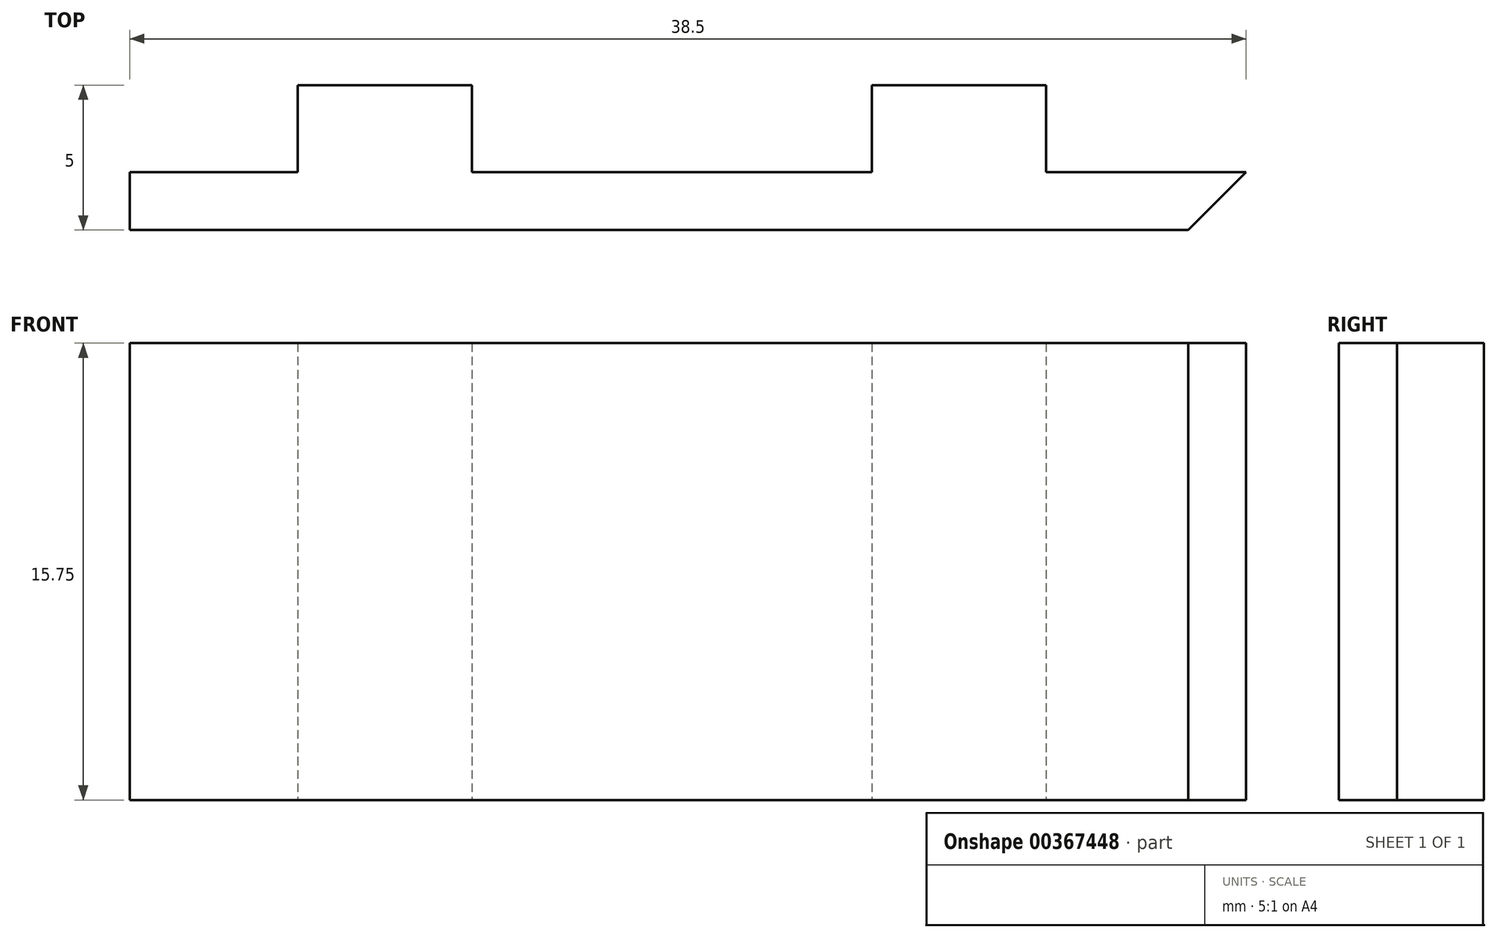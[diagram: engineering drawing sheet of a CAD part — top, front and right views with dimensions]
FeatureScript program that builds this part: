
annotation { "Feature Type Name" : "Feature", "Feature Type Description" : "" }
export const myFeature = defineFeature(function(context is Context, id is Id, definition is map)
    precondition{}
    {
        {
            var Q0;
            Q0=qCreatedBy(makeId("Top.planeOp"),FACE);
            var sketch = newSketch(context, id + "F0", { "sketchPlane" : qUnion([Q0])});
            skLineSegment(sketch, "E0", {"start": v(44.5, 0) * mm, "end": v(44.5, 10) * mm});
            skLineSegment(sketch, "E1", {"start": v(44.5, 10) * mm, "end": v(37.6, 10) * mm});
            skLineSegment(sketch, "E2", {"start": v(37.6, 10) * mm, "end": v(37.6, 16) * mm});
            skLineSegment(sketch, "E3", {"start": v(37.6, 16) * mm, "end": v(31.6, 16) * mm});
            skLineSegment(sketch, "E4", {"start": v(31.6, 16) * mm, "end": v(31.6, 10) * mm});
            skLineSegment(sketch, "E5", {"start": v(31.6, 10) * mm, "end": v(17.8, 10) * mm});
            skLineSegment(sketch, "E6", {"start": v(17.8, 10) * mm, "end": v(17.8, 16) * mm});
            skLineSegment(sketch, "E7", {"start": v(17.8, 16) * mm, "end": v(11.8, 16) * mm});
            skLineSegment(sketch, "E8", {"start": v(11.8, 16) * mm, "end": v(11.8, 10) * mm});
            skLineSegment(sketch, "E9", {"start": v(11.8, 10) * mm, "end": v(0, 10) * mm});
            skLineSegment(sketch, "E10", {"start": v(0, 0) * mm, "end": v(44.5, 0) * mm});
            skLineSegment(sketch, "E11", {"start": v(0, 10) * mm, "end": v(0, 0) * mm});
            skSolve(sketch);
        }
        {
            var Q0;
            Q0=qSketchRegion(id+"F0",true);
            extrude(context, id + "F1", {"entities" : qUnion([Q0]), "depth" : 15.75 * mm});
        }
        {
            var Q0;
            Q0=makeQuery(id+"F1.opExtrude","CAP_FACE",FACE,{"disambiguationData":[OSD([sQuery(id+"F0.wireOp",EDGE,"E0"),sQuery(id+"F0.wireOp",EDGE,"E1"),sQuery(id+"F0.wireOp",EDGE,"E2"),sQuery(id+"F0.wireOp",EDGE,"E3"),sQuery(id+"F0.wireOp",EDGE,"E4"),sQuery(id+"F0.wireOp",EDGE,"E5"),sQuery(id+"F0.wireOp",EDGE,"E6"),sQuery(id+"F0.wireOp",EDGE,"E7"),sQuery(id+"F0.wireOp",EDGE,"E8"),sQuery(id+"F0.wireOp",EDGE,"E9"),sQuery(id+"F0.wireOp",EDGE,"E10"),sQuery(id+"F0.wireOp",EDGE,"E11")])],"isStart":false});
            var sketch = newSketch(context, id + "F2", { "sketchPlane" : qUnion([Q0])});
            skPoint(sketch, "E12", {"position": v(24.7, 5) * mm});
            skPoint(sketch, "E12.positionSnap0", {"position": v(44.5, 5) * mm});
            skPoint(sketch, "E12.positionSnap1", {"position": v(24.7, 10) * mm});
            skSolve(sketch);
        }
        {
            var Q0;
            Q0=sQuery(id+"F2.wireOp",VERTEX,"E12");
            var Q1;
            Q1=makeQuery(id+"F1.opExtrude","SWEPT_BODY",BODY,{"disambiguationData":[OSD([sQuery(id+"F0.wireOp",EDGE,"E0"),sQuery(id+"F0.wireOp",EDGE,"E1"),sQuery(id+"F0.wireOp",EDGE,"E2"),sQuery(id+"F0.wireOp",EDGE,"E3"),sQuery(id+"F0.wireOp",EDGE,"E4"),sQuery(id+"F0.wireOp",EDGE,"E5"),sQuery(id+"F0.wireOp",EDGE,"E6"),sQuery(id+"F0.wireOp",EDGE,"E7"),sQuery(id+"F0.wireOp",EDGE,"E8"),sQuery(id+"F0.wireOp",EDGE,"E9"),sQuery(id+"F0.wireOp",EDGE,"E10"),sQuery(id+"F0.wireOp",EDGE,"E11")])]});
            hole(context, id + "F3", {"style" : HoleStyle.SIMPLE, "endStyle" : HoleEndStyle.THROUGH, "holeDiameter" : 4 * mm, "locations" : qUnion([Q0]), "scope" : qUnion([Q1]), "isTappedThrough" : true});
        }
        {
            var Q0;
            Q0=makeQuery(id+"F1.opExtrude","SWEPT_FACE",FACE,{"disambiguationData":[OSD([sQuery(id+"F0.wireOp",EDGE,"E11")])]});
            extrude(context, id + "F4", {"entities" : qUnion([Q0]), "operationType" : NewBodyOperationType.ADD, "depth" : 3 * mm});
        }
        {
            var Q0;
            {var subQ0=sQuery(id+"F0.wireOp",EDGE,"E9");Q0=makeQuery(id+"F4.boolean.opBoolean","MERGE",FACE,{"derivedFrom":[makeQuery(id+"F1.opExtrude","SWEPT_FACE",FACE,{"disambiguationData":[OSD([subQ0])]}),makeQuery(id+"F4.opExtrude","SWEPT_FACE",FACE,{"disambiguationData":[OSD([subQ0,sQuery(id+"F0.wireOp",EDGE,"E11")])]})]});}
            var sketch = newSketch(context, id + "F5", { "sketchPlane" : qUnion([Q0])});
            skLineSegment(sketch, "E13", {"start": v(0, 0) * mm, "end": v(0, 15.75) * mm});
            skSolve(sketch);
        }
        {
            var Q0;
            {var subQ0=sQuery(id+"F5.wireOp",EDGE,"E13");Q0=makeQuery(id+"F5.imprint","IMPRINT",FACE,{"disambiguationData":[TD([[makeQuery(id+"F5.imprint","IMPRINT",EDGE,{"derivedFrom":subQ0}),-1.0]])]});}
            extrude(context, id + "F6", {"entities" : qUnion([Q0]), "operationType" : NewBodyOperationType.ADD, "depth" : 25 * mm});
        }
        {
            var Q0;
            Q0=makeQuery(id+"F6.opExtrude","SWEPT_FACE",FACE,{"disambiguationData":[OSD([sQuery(id+"F5.wireOp",EDGE,"E13")])]});
            var sketch = newSketch(context, id + "F7", { "sketchPlane" : qUnion([Q0])});
            skPoint(sketch, "E14", {"position": v(27.25, 7.88) * mm});
            skPoint(sketch, "E14.positionSnap0", {"position": v(35, 7.88) * mm});
            skPoint(sketch, "E15", {"position": v(17.75, 7.88) * mm});
            skLineSegment(sketch, "E16", {"start": v(27.25, 7.88) * mm, "end": v(35, 7.88) * mm, "construction": true});
            skLineSegment(sketch, "E17", {"start": v(17.75, 7.88) * mm, "end": v(10, 7.88) * mm, "construction": true});
            skSolve(sketch);
        }
        {
            var Q0;
            Q0=sQuery(id+"F7.wireOp",VERTEX,"E14");
            var Q1;
            Q1=sQuery(id+"F7.wireOp",VERTEX,"E15");
            var Q2;
            Q2=makeQuery(id+"F1.opExtrude","SWEPT_BODY",BODY,{"disambiguationData":[OSD([sQuery(id+"F0.wireOp",EDGE,"E0"),sQuery(id+"F0.wireOp",EDGE,"E1"),sQuery(id+"F0.wireOp",EDGE,"E2"),sQuery(id+"F0.wireOp",EDGE,"E3"),sQuery(id+"F0.wireOp",EDGE,"E4"),sQuery(id+"F0.wireOp",EDGE,"E5"),sQuery(id+"F0.wireOp",EDGE,"E6"),sQuery(id+"F0.wireOp",EDGE,"E7"),sQuery(id+"F0.wireOp",EDGE,"E8"),sQuery(id+"F0.wireOp",EDGE,"E9"),sQuery(id+"F0.wireOp",EDGE,"E10"),sQuery(id+"F0.wireOp",EDGE,"E11")])]});
            hole(context, id + "F8", {"style" : HoleStyle.SIMPLE, "endStyle" : HoleEndStyle.THROUGH, "holeDiameter" : 2 * mm, "startFromSketch" : true, "locations" : qUnion([Q0, Q1]), "scope" : qUnion([Q2]), "isTappedThrough" : true});
        }
        {
            var Q0;
            {var subQ0=sQuery(id+"F0.wireOp",EDGE,"E11");var subQ1=sQuery(id+"F0.wireOp",EDGE,"E9");var subQ2=makeQuery(id+"F4.boolean.opBoolean","MERGE",EDGE,{"derivedFrom":[makeQuery(id+"F1.opExtrude","CAP_EDGE",EDGE,{"disambiguationData":[OSD([subQ1])],"isStart":false}),makeQuery(id+"F4.opExtrude","SWEPT_EDGE",EDGE,{"disambiguationData":[OSD([subQ1,subQ0]),TDD([makeQuery(id+"F1.opExtrude","CAP_VERTEX",VERTEX,{"disambiguationData":[OSD([subQ1,subQ0])],"isStart":false})])]})]});Q0=makeQuery(id+"F6.boolean.opBoolean","MERGE",FACE,{"derivedFrom":[makeQuery(id+"F4.boolean.opBoolean","MERGE",FACE,{"derivedFrom":[makeQuery(id+"F1.opExtrude","CAP_FACE",FACE,{"disambiguationData":[OSD([sQuery(id+"F0.wireOp",EDGE,"E0"),sQuery(id+"F0.wireOp",EDGE,"E1"),sQuery(id+"F0.wireOp",EDGE,"E2"),sQuery(id+"F0.wireOp",EDGE,"E3"),sQuery(id+"F0.wireOp",EDGE,"E4"),sQuery(id+"F0.wireOp",EDGE,"E5"),sQuery(id+"F0.wireOp",EDGE,"E6"),sQuery(id+"F0.wireOp",EDGE,"E7"),sQuery(id+"F0.wireOp",EDGE,"E8"),subQ1,sQuery(id+"F0.wireOp",EDGE,"E10"),subQ0])],"isStart":false}),makeQuery(id+"F4.opExtrude","SWEPT_FACE",FACE,{"disambiguationData":[OSD([subQ0]),TDD([makeQuery(id+"F1.opExtrude","CAP_EDGE",EDGE,{"disambiguationData":[OSD([subQ0])],"isStart":false})])]})]}),makeQuery(id+"F6.opExtrude","SWEPT_FACE",FACE,{"disambiguationData":[OSD([subQ1,subQ0]),TDD([makeQuery(id+"F5.imprint","IMPRINT",EDGE,{"disambiguationData":[TD([[makeQuery(id+"F5.imprint","INTERSECT",VERTEX,{"derivedFrom":[subQ2,sQuery(id+"F5.wireOp",EDGE,"E13")]}),-1.0]])],"derivedFrom":subQ2})])]})]});}
            var sketch = newSketch(context, id + "F9", { "sketchPlane" : qUnion([Q0])});
            skLineSegment(sketch, "E18", {"start": v(0, 10) * mm, "end": v(0, 6) * mm});
            skLineSegment(sketch, "E19", {"start": v(0, 6) * mm, "end": v(6, 6) * mm});
            skLineSegment(sketch, "E20", {"start": v(6, 6) * mm, "end": v(6, 10) * mm});
            skLineSegment(sketch, "E21", {"start": v(6, 10) * mm, "end": v(0, 10) * mm});
            skSolve(sketch);
        }
        {
            var Q0;
            Q0=qSketchRegion(id+"F9",true);
            extrude(context, id + "F10", {"entities" : qUnion([Q0]), "operationType" : NewBodyOperationType.REMOVE, "endBound" : BoundingType.THROUGH_ALL, "oppositeDirection" : true, "depth" : 25 * mm});
        }
        {
            var Q0;
            Q0=makeQuery(id+"F1.opExtrude","SWEPT_EDGE",EDGE,{"disambiguationData":[OSD([sQuery(id+"F0.wireOp",EDGE,"E7"),sQuery(id+"F0.wireOp",EDGE,"E8")])]});
            var Q1;
            Q1=makeQuery(id+"F1.opExtrude","SWEPT_EDGE",EDGE,{"disambiguationData":[OSD([sQuery(id+"F0.wireOp",EDGE,"E6"),sQuery(id+"F0.wireOp",EDGE,"E7")])]});
            var Q2;
            Q2=makeQuery(id+"F1.opExtrude","SWEPT_EDGE",EDGE,{"disambiguationData":[OSD([sQuery(id+"F0.wireOp",EDGE,"E3"),sQuery(id+"F0.wireOp",EDGE,"E4")])]});
            var Q3;
            Q3=makeQuery(id+"F1.opExtrude","SWEPT_EDGE",EDGE,{"disambiguationData":[OSD([sQuery(id+"F0.wireOp",EDGE,"E2"),sQuery(id+"F0.wireOp",EDGE,"E3")])]});
            chamfer(context, id + "F11", {"entities" : qUnion([Q0, Q1, Q2, Q3]), "width" : 1 * mm, "tangentPropagation" : true});
        }
        {
            var Q0;
            Q0=makeQuery(id+"F1.opExtrude","SWEPT_EDGE",EDGE,{"disambiguationData":[OSD([sQuery(id+"F0.wireOp",EDGE,"E0"),sQuery(id+"F0.wireOp",EDGE,"E10")])]});
            chamfer(context, id + "F12", {"entities" : qUnion([Q0]), "width" : 5 * mm, "tangentPropagation" : true});
        }
        {
            var Q0;
            {var subQ0=sQuery(id+"F0.wireOp",EDGE,"E11");var subQ1=sQuery(id+"F0.wireOp",EDGE,"E9");Q0=makeQuery(id+"F6.boolean.opBoolean","MERGE",FACE,{"derivedFrom":[makeQuery(id+"F4.opExtrude","CAP_FACE",FACE,{"disambiguationData":[OSD([subQ0])],"isStart":false}),makeQuery(id+"F6.opExtrude","SWEPT_FACE",FACE,{"disambiguationData":[OSD([subQ1,subQ0]),TDD([makeQuery(id+"F5.imprint","IMPRINT",EDGE,{"derivedFrom":makeQuery(id+"F4.opExtrude","CAP_EDGE",EDGE,{"disambiguationData":[OSD([subQ1,subQ0])],"isStart":false})})])]})]});}
            extrude(context, id + "F13", {"entities" : qUnion([Q0]), "operationType" : NewBodyOperationType.ADD, "depth" : 1 * mm});
        }
        {
            var Q0;
            Q0=makeQuery(id+"F10.boolean.opBoolean","MERGE",FACE,{"derivedFrom":[makeQuery(id+"F6.opExtrude","SWEPT_FACE",FACE,{"disambiguationData":[OSD([sQuery(id+"F5.wireOp",EDGE,"E13")])]}),makeQuery(id+"F10.opExtrude","SWEPT_FACE",FACE,{"disambiguationData":[OSD([sQuery(id+"F9.wireOp",EDGE,"E18")])]})]});
            extrude(context, id + "F14", {"entities" : qUnion([Q0]), "operationType" : NewBodyOperationType.REMOVE, "oppositeDirection" : true, "depth" : 1 * mm});
        }
        {
            var Q0;
            {var subQ0=sQuery(id+"F0.wireOp",EDGE,"E11");var subQ1=sQuery(id+"F0.wireOp",EDGE,"E9");var subQ2=makeQuery(id+"F4.boolean.opBoolean","MERGE",EDGE,{"derivedFrom":[makeQuery(id+"F1.opExtrude","CAP_EDGE",EDGE,{"disambiguationData":[OSD([subQ1])],"isStart":false}),makeQuery(id+"F4.opExtrude","SWEPT_EDGE",EDGE,{"disambiguationData":[OSD([subQ1,subQ0]),TDD([makeQuery(id+"F1.opExtrude","CAP_VERTEX",VERTEX,{"disambiguationData":[OSD([subQ1,subQ0])],"isStart":false})])]})]});var subQ3=makeQuery(id+"F5.imprint","INTERSECT",VERTEX,{"derivedFrom":[makeQuery(id+"F4.opExtrude","CAP_EDGE",EDGE,{"disambiguationData":[OSD([subQ1,subQ0])],"isStart":false}),subQ2]});var subQ4=makeQuery(id+"F1.opExtrude","CAP_EDGE",EDGE,{"disambiguationData":[OSD([subQ0])],"isStart":false});Q0=makeQuery(id+"F13.boolean.opBoolean","MERGE",FACE,{"derivedFrom":[makeQuery(id+"F6.boolean.opBoolean","MERGE",FACE,{"derivedFrom":[makeQuery(id+"F4.boolean.opBoolean","MERGE",FACE,{"derivedFrom":[makeQuery(id+"F1.opExtrude","CAP_FACE",FACE,{"disambiguationData":[OSD([sQuery(id+"F0.wireOp",EDGE,"E0"),sQuery(id+"F0.wireOp",EDGE,"E1"),sQuery(id+"F0.wireOp",EDGE,"E2"),sQuery(id+"F0.wireOp",EDGE,"E3"),sQuery(id+"F0.wireOp",EDGE,"E4"),sQuery(id+"F0.wireOp",EDGE,"E5"),sQuery(id+"F0.wireOp",EDGE,"E6"),sQuery(id+"F0.wireOp",EDGE,"E7"),sQuery(id+"F0.wireOp",EDGE,"E8"),subQ1,sQuery(id+"F0.wireOp",EDGE,"E10"),subQ0])],"isStart":false}),makeQuery(id+"F4.opExtrude","SWEPT_FACE",FACE,{"disambiguationData":[OSD([subQ0]),TDD([subQ4])]})]}),makeQuery(id+"F6.opExtrude","SWEPT_FACE",FACE,{"disambiguationData":[OSD([subQ1,subQ0]),TDD([makeQuery(id+"F5.imprint","IMPRINT",EDGE,{"disambiguationData":[TD([[makeQuery(id+"F5.imprint","INTERSECT",VERTEX,{"derivedFrom":[subQ2,sQuery(id+"F5.wireOp",EDGE,"E13")]}),-1.0]])],"derivedFrom":subQ2})])]})]}),makeQuery(id+"F13.opExtrude","SWEPT_FACE",FACE,{"disambiguationData":[OSD([subQ1,subQ0]),TDD([makeQuery(id+"F6.boolean.opBoolean","MERGE",EDGE,{"derivedFrom":[makeQuery(id+"F4.opExtrude","CAP_EDGE",EDGE,{"disambiguationData":[OSD([subQ0]),TDD([subQ4])],"isStart":false}),makeQuery(id+"F6.opExtrude","SWEPT_EDGE",EDGE,{"disambiguationData":[OSD([subQ1,subQ0]),TDD([subQ3])]})]})])]})]});}
            var sketch = newSketch(context, id + "F15", { "sketchPlane" : qUnion([Q0])});
            skLineSegment(sketch, "E22.bottom", {"start": v(5.9, 13) * mm, "end": v(43, 13) * mm});
            skLineSegment(sketch, "E22.top", {"start": v(5.9, 24.45) * mm, "end": v(43, 24.45) * mm});
            skLineSegment(sketch, "E22.left", {"start": v(5.9, 13) * mm, "end": v(5.9, 24.45) * mm});
            skLineSegment(sketch, "E22.right", {"start": v(43, 13) * mm, "end": v(43, 24.45) * mm});
            skLineSegment(sketch, "E23.bottom", {"start": v(-12.85, -2.88) * mm, "end": v(6, -2.88) * mm});
            skLineSegment(sketch, "E23.top", {"start": v(-12.85, 35.56) * mm, "end": v(6, 35.56) * mm});
            skLineSegment(sketch, "E23.left", {"start": v(-12.85, -2.88) * mm, "end": v(-12.85, 35.56) * mm});
            skLineSegment(sketch, "E23.right", {"start": v(6, -2.88) * mm, "end": v(6, 35.56) * mm});
            skLineSegment(sketch, "E24.bottom", {"start": v(49.35, -4.45) * mm, "end": v(6, -4.45) * mm});
            skLineSegment(sketch, "E24.top", {"start": v(49.35, 8) * mm, "end": v(6, 8) * mm});
            skLineSegment(sketch, "E24.left", {"start": v(49.35, -4.45) * mm, "end": v(49.35, 8) * mm});
            skLineSegment(sketch, "E24.right", {"start": v(6, -4.45) * mm, "end": v(6, 8) * mm});
            skSolve(sketch);
        }
        {
            var Q0;
            Q0=qSketchRegion(id+"F15",true);
            extrude(context, id + "F16", {"entities" : qUnion([Q0]), "operationType" : NewBodyOperationType.REMOVE, "endBound" : BoundingType.THROUGH_ALL, "oppositeDirection" : true, "depth" : 25 * mm});
        }
        {
            var Q0;
            Q0=makeQuery(id+"F16.boolean.opBoolean","COPY",EDGE,{"derivedFrom":makeQuery(id+"F16.opExtrude","SWEPT_EDGE",EDGE,{"disambiguationData":[OSD([sQuery(id+"F15.wireOp",EDGE,"E23.right"),sQuery(id+"F15.wireOp",EDGE,"E24.top"),sQuery(id+"F15.wireOp",EDGE,"E24.right")])]})});
            var Q1;
            Q1=makeQuery(id+"F16.boolean.opBoolean","INTERSECT",EDGE,{"derivedFrom":[makeQuery(id+"F1.opExtrude","SWEPT_FACE",FACE,{"disambiguationData":[OSD([sQuery(id+"F0.wireOp",EDGE,"E0")])]}),makeQuery(id+"F16.opExtrude","SWEPT_FACE",FACE,{"disambiguationData":[OSD([sQuery(id+"F15.wireOp",EDGE,"E24.top")])]})]});
            chamfer(context, id + "F17", {"entities" : qUnion([Q0, Q1]), "width" : 2 * mm, "tangentPropagation" : true});
        }
    });
